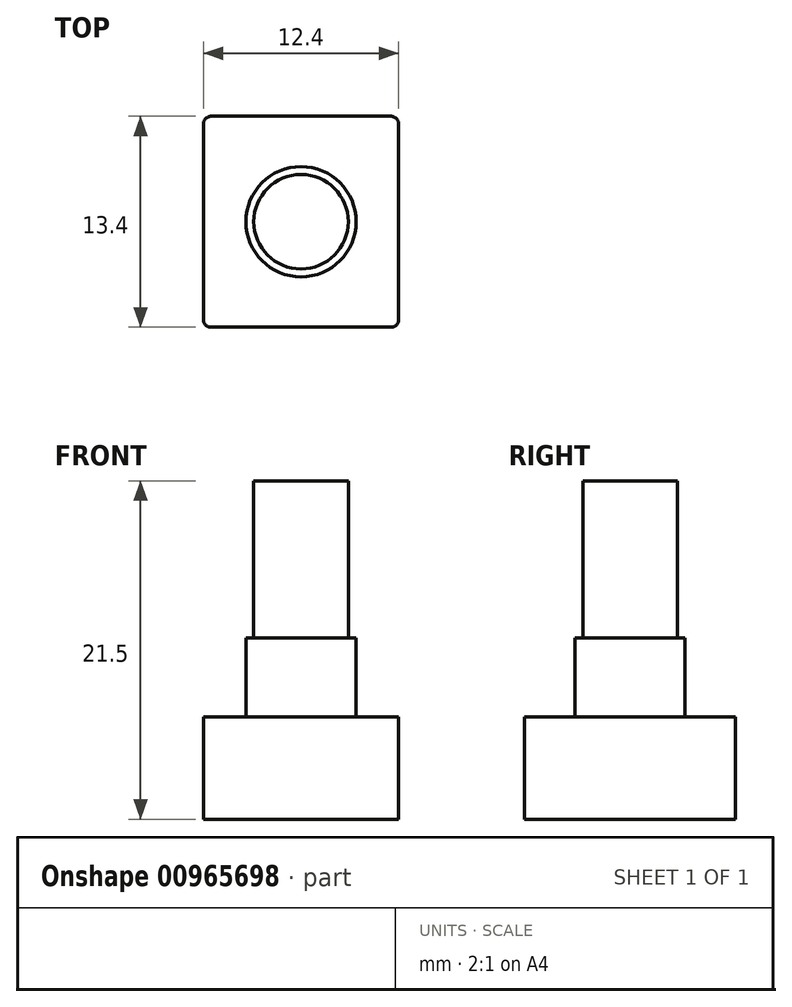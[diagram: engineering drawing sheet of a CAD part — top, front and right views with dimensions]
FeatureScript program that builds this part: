
annotation { "Feature Type Name" : "Feature", "Feature Type Description" : "" }
export const myFeature = defineFeature(function(context is Context, id is Id, definition is map)
    precondition{}
    {
        {
            var Q0;
            Q0=qCreatedBy(makeId("Top.planeOp"),FACE);
            var sketch = newSketch(context, id + "F0", { "sketchPlane" : qUnion([Q0])});
            skLineSegment(sketch, "E0.bottom", {"start": v(5.7, 6.7) * mm, "end": v(-5.7, 6.7) * mm});
            skLineSegment(sketch, "E0.top", {"start": v(5.7, -6.7) * mm, "end": v(-5.7, -6.7) * mm});
            skLineSegment(sketch, "E0.left", {"start": v(6.2, 6.2) * mm, "end": v(6.2, -6.2) * mm});
            skLineSegment(sketch, "E0.right", {"start": v(-6.2, 6.2) * mm, "end": v(-6.2, -6.2) * mm});
            skPoint(sketch, "E0.middle", {"position": v(0, 0) * mm});
            skPoint(sketch, "E1.visualSharp", {"position": v(-6.2, 6.7) * mm});
            skArc(sketch, "E1.filletArc", {"start": v(-5.7, 6.7) * mm, "mid": v(-6.05, 6.55) * mm, "end": v(-6.2, 6.2) * mm});
            skPoint(sketch, "E2.visualSharp", {"position": v(6.2, 6.7) * mm});
            skArc(sketch, "E2.filletArc", {"start": v(6.2, 6.2) * mm, "mid": v(6.05, 6.55) * mm, "end": v(5.7, 6.7) * mm});
            skPoint(sketch, "E3.visualSharp", {"position": v(6.2, -6.7) * mm});
            skArc(sketch, "E3.filletArc", {"start": v(5.7, -6.7) * mm, "mid": v(6.05, -6.55) * mm, "end": v(6.2, -6.2) * mm});
            skPoint(sketch, "E4.visualSharp", {"position": v(-6.2, -6.7) * mm});
            skArc(sketch, "E4.filletArc", {"start": v(-6.2, -6.2) * mm, "mid": v(-6.05, -6.55) * mm, "end": v(-5.7, -6.7) * mm});
            skSolve(sketch);
        }
        {
            var Q0;
            Q0=qSketchRegion(id+"F0",true);
            extrude(context, id + "F1", {"entities" : qUnion([Q0]), "depth" : 6.5 * mm, "offsetDistance" : 25 * mm});
        }
        {
            var Q0;
            Q0=makeQuery(id+"F1.opExtrude","CAP_FACE",FACE,{"disambiguationData":[OSD([sQuery(id+"F0.wireOp",EDGE,"E0.bottom"),sQuery(id+"F0.wireOp",EDGE,"E0.top"),sQuery(id+"F0.wireOp",EDGE,"E0.left"),sQuery(id+"F0.wireOp",EDGE,"E0.right"),sQuery(id+"F0.wireOp",EDGE,"E1.filletArc"),sQuery(id+"F0.wireOp",EDGE,"E2.filletArc"),sQuery(id+"F0.wireOp",EDGE,"E3.filletArc"),sQuery(id+"F0.wireOp",EDGE,"E4.filletArc")])],"isStart":false});
            var sketch = newSketch(context, id + "F2", { "sketchPlane" : qUnion([Q0])});
            skCircle(sketch, "E5", {"center": v(0, 0) * mm, "radius": 3.5 * mm});
            skSolve(sketch);
        }
        {
            var Q0;
            Q0=qSketchRegion(id+"F2",true);
            extrude(context, id + "F3", {"entities" : qUnion([Q0]), "operationType" : NewBodyOperationType.ADD, "depth" : 5 * mm, "offsetDistance" : 25 * mm});
        }
        {
            var Q0;
            Q0=makeQuery(id+"F1.opExtrude","CAP_FACE",FACE,{"disambiguationData":[OSD([sQuery(id+"F0.wireOp",EDGE,"E0.bottom"),sQuery(id+"F0.wireOp",EDGE,"E0.top"),sQuery(id+"F0.wireOp",EDGE,"E0.left"),sQuery(id+"F0.wireOp",EDGE,"E0.right"),sQuery(id+"F0.wireOp",EDGE,"E1.filletArc"),sQuery(id+"F0.wireOp",EDGE,"E2.filletArc"),sQuery(id+"F0.wireOp",EDGE,"E3.filletArc"),sQuery(id+"F0.wireOp",EDGE,"E4.filletArc")])],"isStart":false});
            var sketch = newSketch(context, id + "F4", { "sketchPlane" : qUnion([Q0])});
            skCircle(sketch, "E6", {"center": v(0, 0) * mm, "radius": 3 * mm});
            skSolve(sketch);
        }
        {
            var Q0;
            Q0=qSketchRegion(id+"F4",true);
            extrude(context, id + "F5", {"entities" : qUnion([Q0]), "operationType" : NewBodyOperationType.ADD, "depth" : 15 * mm, "offsetDistance" : 25 * mm});
        }
    });
